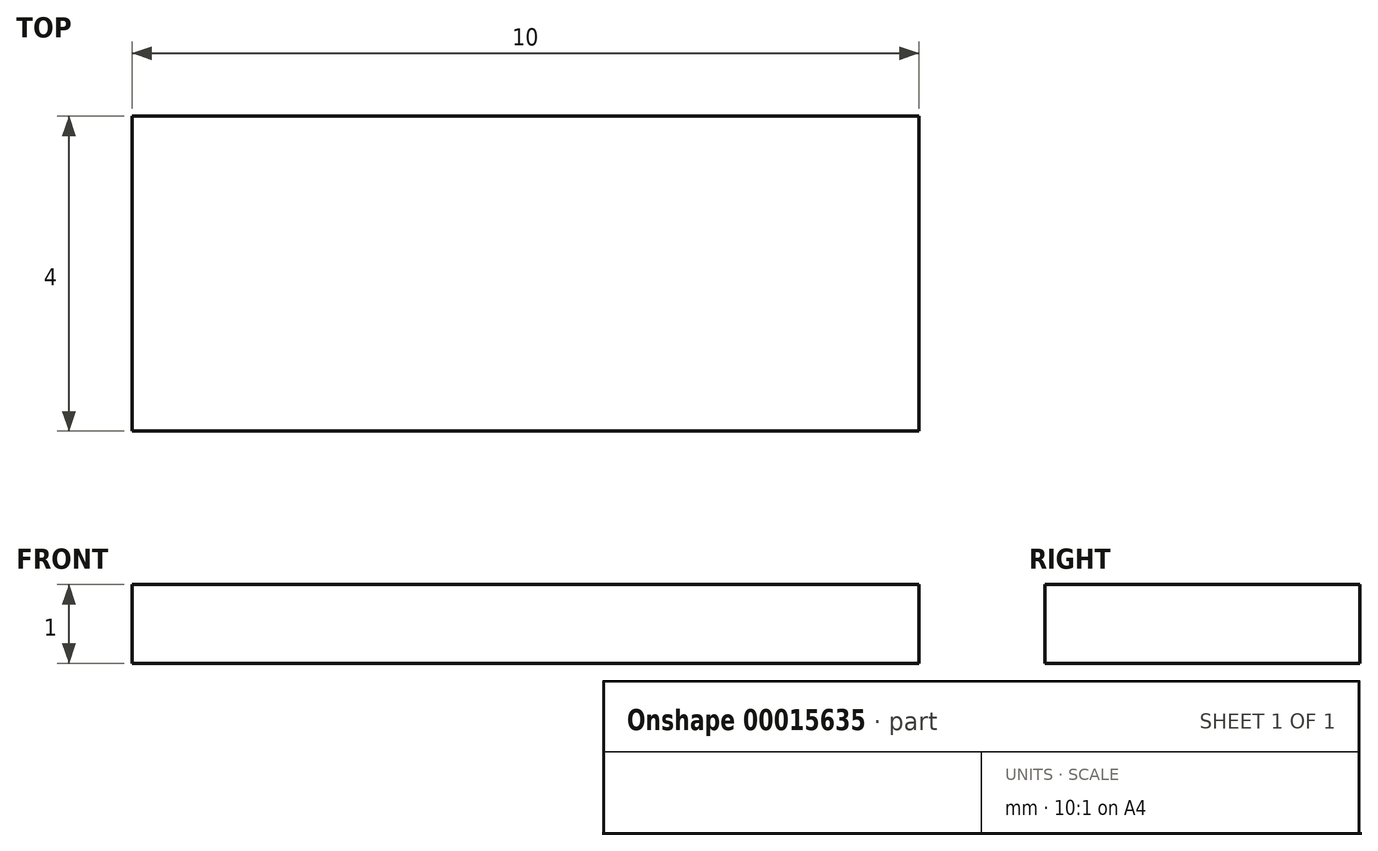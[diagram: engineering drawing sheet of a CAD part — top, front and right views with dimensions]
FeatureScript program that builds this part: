
annotation { "Feature Type Name" : "Feature", "Feature Type Description" : "" }
export const myFeature = defineFeature(function(context is Context, id is Id, definition is map)
    precondition{}
    {
        {
            var Q0;
            Q0=qCreatedBy(makeId("Top.planeOp"),FACE);
            var sketch = newSketch(context, id + "F0", { "sketchPlane" : qUnion([Q0])});
            skLineSegment(sketch, "E0.rect.bottom", {"start": v(5, 2) * mm, "end": v(-5, 2) * mm});
            skLineSegment(sketch, "E0.rect.top", {"start": v(5, -2) * mm, "end": v(-5, -2) * mm});
            skLineSegment(sketch, "E0.rect.left", {"start": v(5, 2) * mm, "end": v(5, -2) * mm});
            skLineSegment(sketch, "E0.rect.right", {"start": v(-5, 2) * mm, "end": v(-5, -2) * mm});
            skPoint(sketch, "E0.rect.middle", {"position": v(0, 0) * mm});
            skSolve(sketch);
        }
        {
            var Q0;
            Q0=makeQuery(id+"F0.imprint","IMPRINT",FACE,{"disambiguationData":[TD([[makeQuery(id+"F0.imprint","IMPRINT",EDGE,{"derivedFrom":sQuery(id+"F0.wireOp",EDGE,"E0.rect.bottom")}),1.0]])]});
            extrude(context, id + "F1", {"entities" : qUnion([Q0]), "depth" : 1 * mm});
        }
    });
